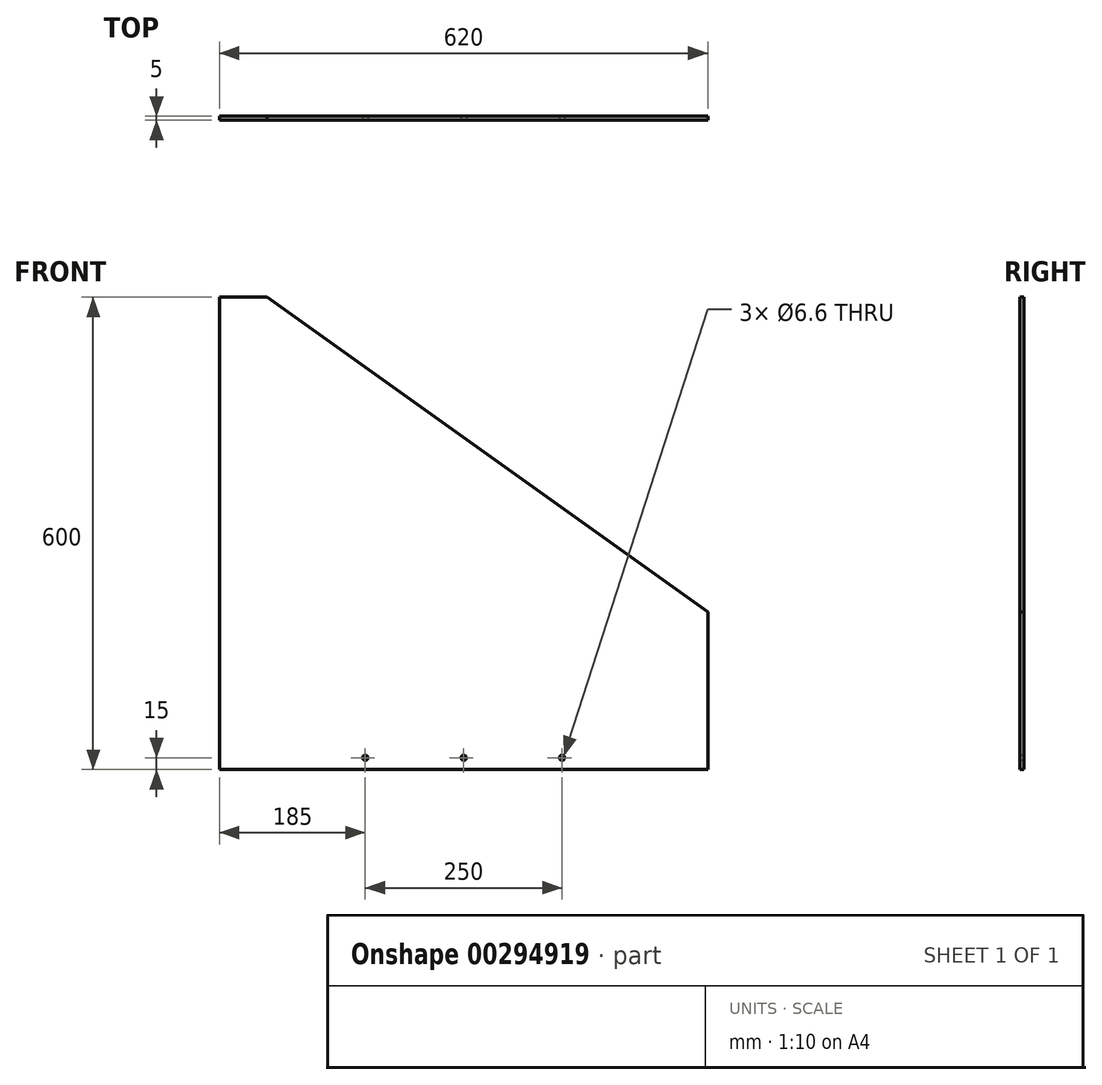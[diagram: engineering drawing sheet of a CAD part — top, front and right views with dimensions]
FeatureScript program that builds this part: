
annotation { "Feature Type Name" : "Feature", "Feature Type Description" : "" }
export const myFeature = defineFeature(function(context is Context, id is Id, definition is map)
    precondition{}
    {
        {
            var Q0;
            Q0=qCreatedBy(makeId("Front.planeOp"),FACE);
            var sketch = newSketch(context, id + "F0", { "sketchPlane" : qUnion([Q0])});
            skLineSegment(sketch, "E0.bottom", {"start": v(-310, 300) * mm, "end": v(310, 300) * mm});
            skLineSegment(sketch, "E0.top", {"start": v(-310, -300) * mm, "end": v(310, -300) * mm});
            skLineSegment(sketch, "E0.left", {"start": v(-310, 300) * mm, "end": v(-310, -300) * mm});
            skLineSegment(sketch, "E0.right", {"start": v(310, 300) * mm, "end": v(310, -300) * mm});
            skPoint(sketch, "E0.middle", {"position": v(0, 0) * mm});
            skLineSegment(sketch, "E1", {"start": v(-250, 300) * mm, "end": v(-250, -300) * mm, "construction": true});
            skLineSegment(sketch, "E2", {"start": v(-310, -100) * mm, "end": v(310, -100) * mm, "construction": true});
            skLineSegment(sketch, "E3", {"start": v(-250, 300) * mm, "end": v(310, -100) * mm});
            skSolve(sketch);
        }
        {
            var Q0;
            {var subQ1=sQuery(id+"F0.wireOp",EDGE,"E0.top");Q0=makeQuery(id+"F0.imprint","IMPRINT",FACE,{"disambiguationData":[TD([[makeQuery(id+"F0.imprint","IMPRINT",EDGE,{"derivedFrom":subQ1}),1.0]])]});}
            extrude(context, id + "F1", {"entities" : qUnion([Q0]), "depth" : 5 * mm, "offsetDistance" : 25 * mm});
        }
        {
            var Q0;
            Q0=makeQuery(id+"F1.opExtrude","CAP_FACE",FACE,{"disambiguationData":[OSD([sQuery(id+"F0.wireOp",EDGE,"E0.bottom"),sQuery(id+"F0.wireOp",EDGE,"E0.top"),sQuery(id+"F0.wireOp",EDGE,"E0.left"),sQuery(id+"F0.wireOp",EDGE,"E0.right"),sQuery(id+"F0.wireOp",EDGE,"E3")])],"isStart":false});
            var sketch = newSketch(context, id + "F2", { "sketchPlane" : qUnion([Q0])});
            skLineSegment(sketch, "E4", {"start": v(-310, -285) * mm, "end": v(310, -285) * mm, "construction": true});
            skLineSegment(sketch, "E5", {"start": v(-250, 300) * mm, "end": v(-250, -300) * mm, "construction": true});
            skPoint(sketch, "E6", {"position": v(-125, -285) * mm});
            skPoint(sketch, "E7", {"position": v(0, -285) * mm});
            skPoint(sketch, "E8", {"position": v(125, -285) * mm});
            skSolve(sketch);
        }
        {
            var Q0;
            Q0=sQuery(id+"F2.wireOp",VERTEX,"E6");
            var Q1;
            Q1=sQuery(id+"F2.wireOp",VERTEX,"E7");
            var Q2;
            Q2=sQuery(id+"F2.wireOp",VERTEX,"E8");
            var Q3;
            Q3=makeQuery(id+"F1.opExtrude","SWEPT_BODY",BODY,{"disambiguationData":[OSD([sQuery(id+"F0.wireOp",EDGE,"E0.bottom"),sQuery(id+"F0.wireOp",EDGE,"E0.top"),sQuery(id+"F0.wireOp",EDGE,"E0.left"),sQuery(id+"F0.wireOp",EDGE,"E0.right"),sQuery(id+"F0.wireOp",EDGE,"E3")])]});
            hole(context, id + "F3", {"style" : HoleStyle.SIMPLE, "endStyle" : HoleEndStyle.THROUGH, "standardTappedOrClearance" : lookupTablePath({ "standard" : "ISO", "fit" : "Normal", "size" : "M6", "type" : "Clearance" }), "standardBlindInLast" : lookupTablePath({ "fit" : "Standard", "standard" : "ISO", "size" : "M6", "type" : "Clearance" }), "holeDiameter" : 6.6 * mm, "isTappedThrough" : true, "tappedDepth" : 12 * mm, "tapClearance" : 3, "locations" : qUnion([Q0, Q1, Q2]), "scope" : qUnion([Q3])});
        }
    });
